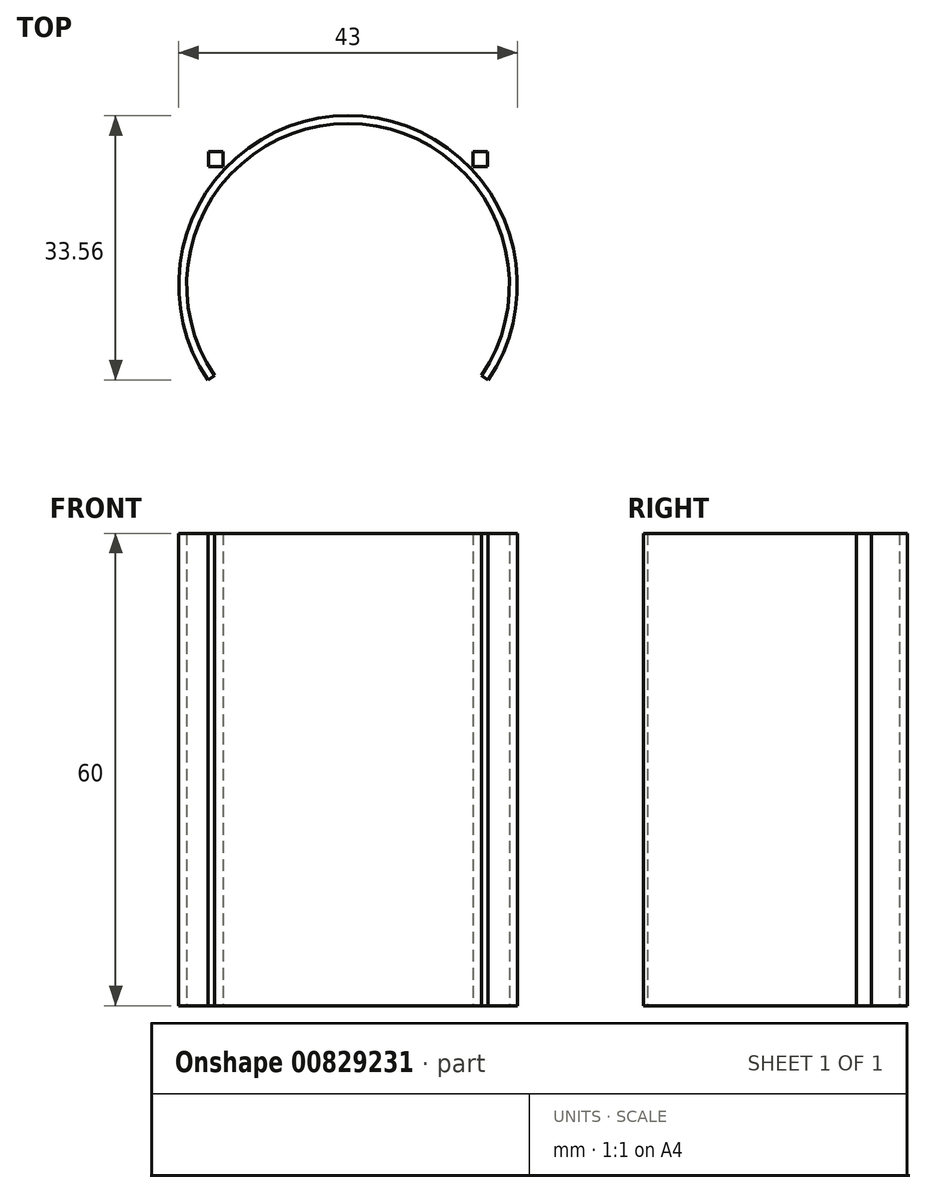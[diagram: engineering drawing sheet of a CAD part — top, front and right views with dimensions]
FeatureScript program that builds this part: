
annotation { "Feature Type Name" : "Feature", "Feature Type Description" : "" }
export const myFeature = defineFeature(function(context is Context, id is Id, definition is map)
    precondition{}
    {
        {
            var Q0;
            Q0=qCreatedBy(makeId("Top.planeOp"),FACE);
            var sketch = newSketch(context, id + "F0", { "sketchPlane" : qUnion([Q0])});
            skArc(sketch, "E0", {"start": v(16.96, -11.51) * mm, "mid": v(0, 20.5) * mm, "end": v(-16.96, -11.51) * mm});
            skArc(sketch, "E1.0", {"start": v(17.8, -12.06) * mm, "mid": v(0, 21.5) * mm, "end": v(-17.8, -12.06) * mm});
            skLineSegment(sketch, "E2", {"start": v(17.8, -12.06) * mm, "end": v(16.96, -11.51) * mm});
            skLineSegment(sketch, "E3.MirrorCS", {"start": v(-17.8, -12.06) * mm, "end": v(-16.96, -11.51) * mm});
            skPoint(sketch, "E4.start.orphan", {"position": v(0, -22.75) * mm});
            skCircle(sketch, "E5", {"center": v(0, 0) * mm, "radius": 24.5 * mm});
            skLineSegment(sketch, "E6.bottom", {"start": v(15.87, 15.03) * mm, "end": v(17.69, 15.03) * mm});
            skLineSegment(sketch, "E6.top", {"start": v(15.87, 16.95) * mm, "end": v(17.69, 16.95) * mm});
            skLineSegment(sketch, "E6.left", {"start": v(15.87, 15.03) * mm, "end": v(15.87, 16.95) * mm});
            skLineSegment(sketch, "E6.right", {"start": v(17.69, 15.03) * mm, "end": v(17.69, 16.95) * mm});
            skLineSegment(sketch, "E7", {"start": v(0, 11.7) * mm, "end": v(0, 19.59) * mm});
            skLineSegment(sketch, "E8.MirrorCS", {"start": v(-15.87, 15.03) * mm, "end": v(-15.87, 16.95) * mm});
            skLineSegment(sketch, "E9.MirrorCS", {"start": v(-15.87, 15.03) * mm, "end": v(-17.69, 15.03) * mm});
            skLineSegment(sketch, "E10.MirrorCS", {"start": v(-17.69, 15.03) * mm, "end": v(-17.69, 16.95) * mm});
            skLineSegment(sketch, "E11.MirrorCS", {"start": v(-15.87, 16.95) * mm, "end": v(-17.69, 16.95) * mm});
            skSolve(sketch);
        }
        {
            var Q0;
            Q0=makeQuery(id+"F0.imprint","IMPRINT",FACE,{"disambiguationData":[TD([[makeQuery(id+"F0.imprint","IMPRINT",EDGE,{"derivedFrom":sQuery(id+"F0.wireOp",EDGE,"E0")}),-1.0]])]});
            extrude(context, id + "F1", {"entities" : qUnion([Q0]), "depth" : 60 * mm, "offsetDistance" : 25 * mm});
        }
        {
            var Q0;
            Q0=makeQuery(id+"F0.imprint","IMPRINT",FACE,{"disambiguationData":[TD([[makeQuery(id+"F0.imprint","IMPRINT",EDGE,{"derivedFrom":sQuery(id+"F0.wireOp",EDGE,"E8.MirrorCS")}),1.0]])]});
            extrude(context, id + "F2", {"entities" : qUnion([Q0]), "depth" : 60 * mm, "offsetDistance" : 25 * mm});
        }
        {
            var Q0;
            Q0=makeQuery(id+"F0.imprint","IMPRINT",FACE,{"disambiguationData":[TD([[makeQuery(id+"F0.imprint","IMPRINT",EDGE,{"derivedFrom":sQuery(id+"F0.wireOp",EDGE,"E6.bottom")}),1.0]])]});
            extrude(context, id + "F3", {"entities" : qUnion([Q0]), "depth" : 60 * mm, "offsetDistance" : 25 * mm});
        }
    });
